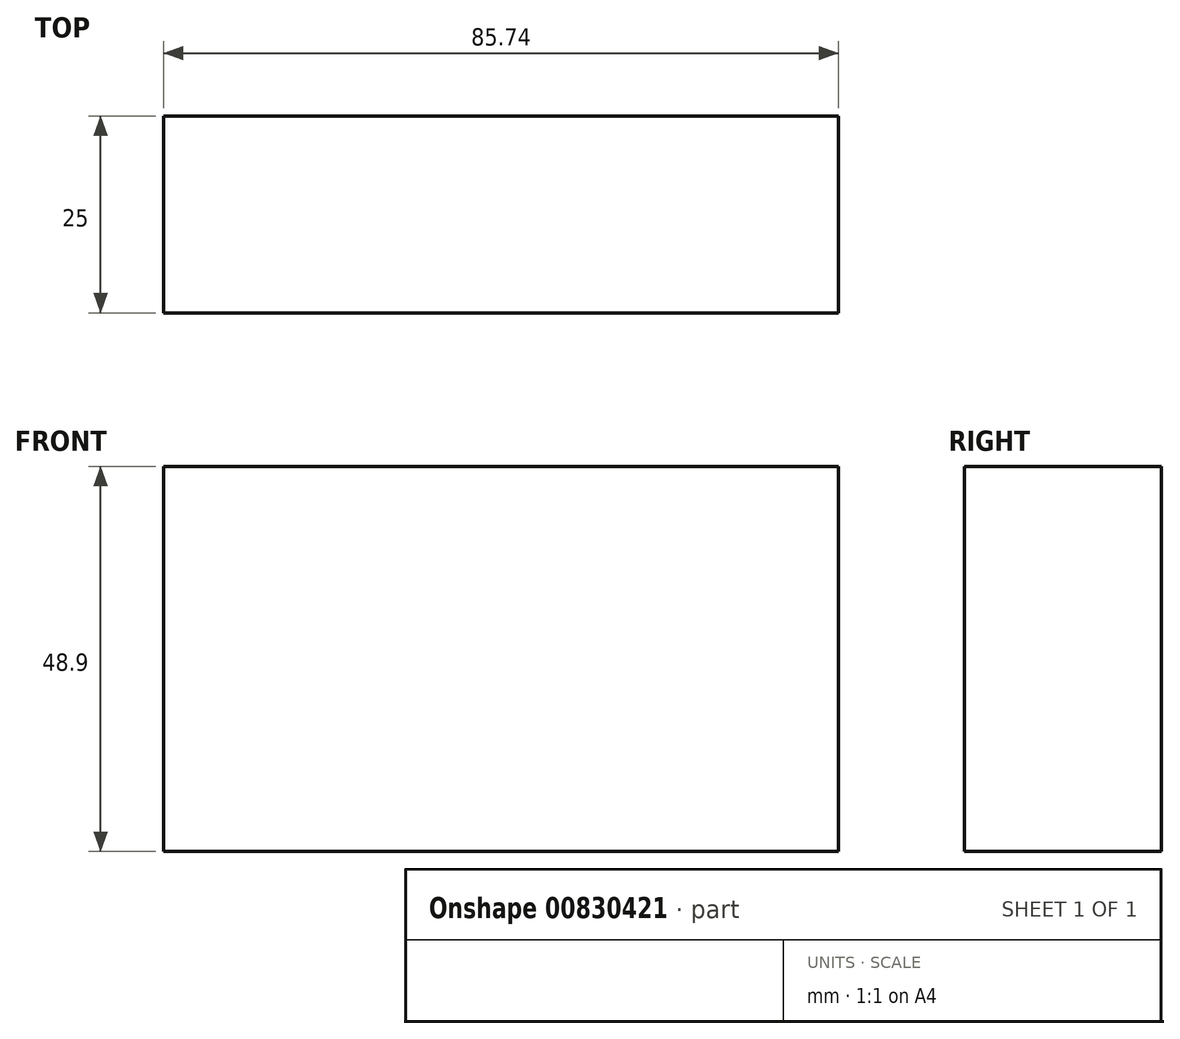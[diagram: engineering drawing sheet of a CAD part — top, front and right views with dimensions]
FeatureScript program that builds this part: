
annotation { "Feature Type Name" : "Feature", "Feature Type Description" : "" }
export const myFeature = defineFeature(function(context is Context, id is Id, definition is map)
    precondition{}
    {
        {
            var Q0;
            Q0=qCreatedBy(makeId("Front.planeOp"),FACE);
            var sketch = newSketch(context, id + "F0", { "sketchPlane" : qUnion([Q0])});
            skLineSegment(sketch, "E0.bottom", {"start": v(0, 0) * mm, "end": v(85.74, 0) * mm});
            skLineSegment(sketch, "E0.top", {"start": v(0, 48.9) * mm, "end": v(85.74, 48.9) * mm});
            skLineSegment(sketch, "E0.left", {"start": v(0, 0) * mm, "end": v(0, 48.9) * mm});
            skLineSegment(sketch, "E0.right", {"start": v(85.74, 0) * mm, "end": v(85.74, 48.9) * mm});
            skSolve(sketch);
        }
        {
            var Q0;
            Q0=makeQuery(id+"F0.imprint","IMPRINT",FACE,{"disambiguationData":[TD([[makeQuery(id+"F0.imprint","IMPRINT",EDGE,{"derivedFrom":sQuery(id+"F0.wireOp",EDGE,"E0.bottom")}),1.0]])]});
            extrude(context, id + "F1", {"entities" : qUnion([Q0]), "depth" : 25 * mm, "offsetDistance" : 25 * mm});
        }
    });
